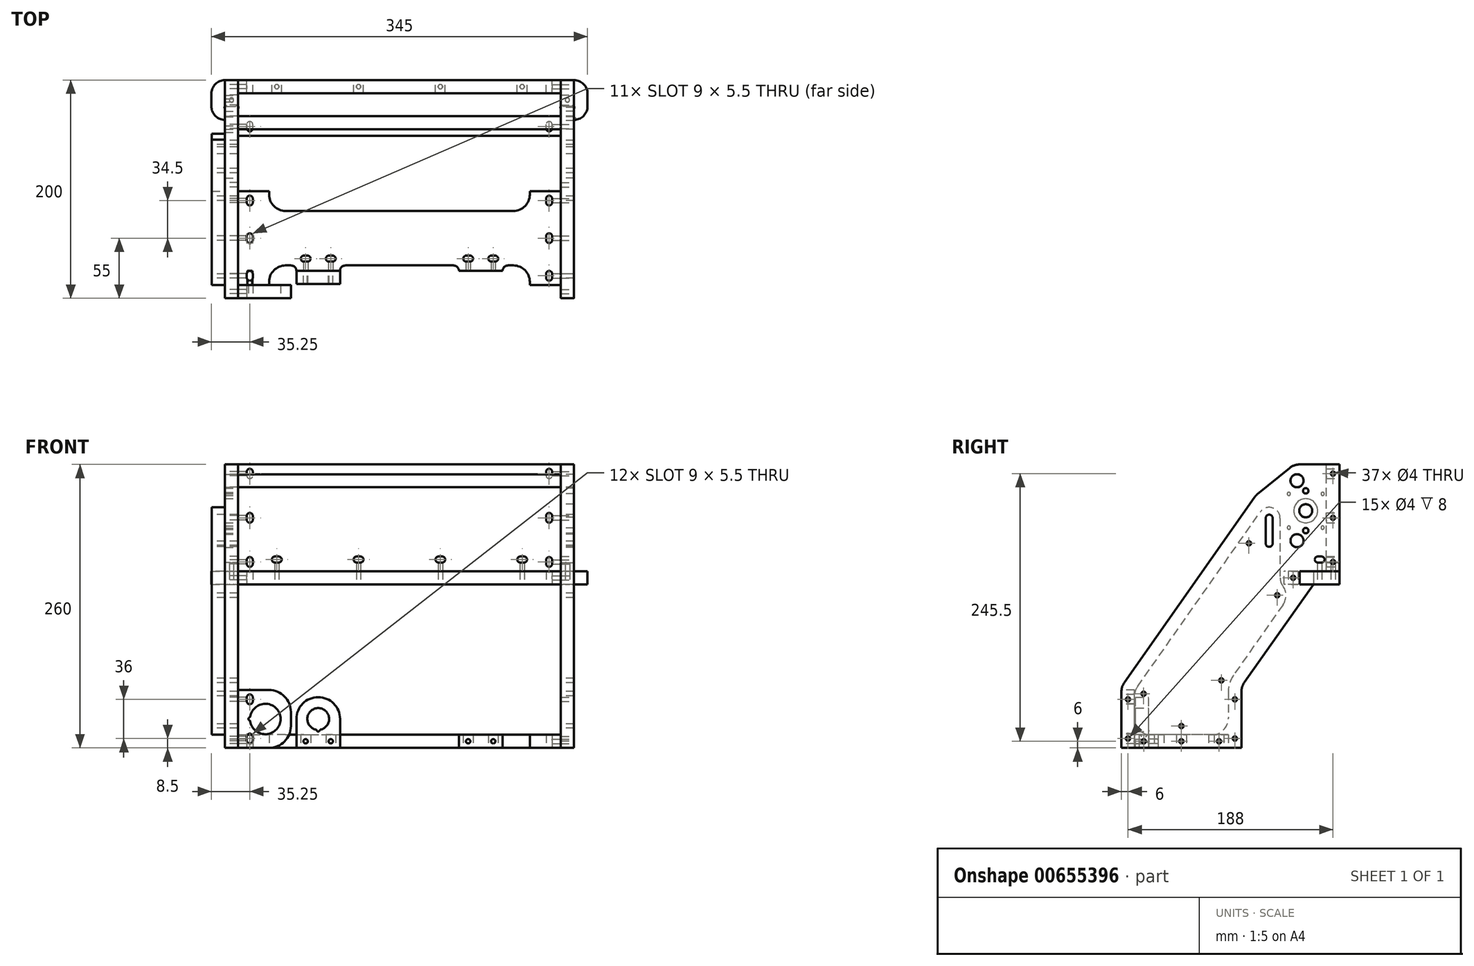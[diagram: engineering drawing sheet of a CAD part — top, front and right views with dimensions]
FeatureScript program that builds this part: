
annotation { "Feature Type Name" : "Feature", "Feature Type Description" : "" }
export const myFeature = defineFeature(function(context is Context, id is Id, definition is map)
    precondition{}
    {
        {
            var Q0;
            Q0=qCreatedBy(makeId("Front.planeOp"),FACE);
            var sketch = newSketch(context, id + "F0", { "sketchPlane" : qUnion([Q0])});
            skLineSegment(sketch, "E0.bottom", {"start": v(-148, 0) * mm, "end": v(148, 0) * mm});
            skLineSegment(sketch, "E0.top", {"start": v(-148, 98) * mm, "end": v(148, 98) * mm});
            skLineSegment(sketch, "E0.left", {"start": v(-148, 0) * mm, "end": v(-148, 98) * mm});
            skLineSegment(sketch, "E0.right", {"start": v(148, 0) * mm, "end": v(148, 98) * mm});
            skSolve(sketch);
        }
        {
            var Q0;
            Q0=qSketchRegion(id+"F0",true);
            extrude(context, id + "F1", {"entities" : qUnion([Q0]), "depth" : 12 * mm, "offsetDistance" : 25 * mm});
        }
        {
            var Q0;
            Q0=makeQuery(id+"F1.opExtrude","SWEPT_FACE",FACE,{"disambiguationData":[OSD([sQuery(id+"F0.wireOp",EDGE,"E0.left")])]});
            var sketch = newSketch(context, id + "F2", { "sketchPlane" : qUnion([Q0])});
            skLineSegment(sketch, "E1.bottom", {"start": v(0, 98) * mm, "end": v(56.7, 98) * mm});
            skLineSegment(sketch, "E1.top", {"start": v(90, -162) * mm, "end": v(200, -162) * mm});
            skLineSegment(sketch, "E1.right", {"start": v(56.7, 98) * mm, "end": v(200, -105.92) * mm});
            skLineSegment(sketch, "E2", {"start": v(200, -162) * mm, "end": v(200, -105.92) * mm});
            skLineSegment(sketch, "E3", {"start": v(24, -12) * mm, "end": v(90, -105.92) * mm});
            skLineSegment(sketch, "E4", {"start": v(0, 0) * mm, "end": v(0, 98) * mm});
            skLineSegment(sketch, "E5", {"start": v(90, -162) * mm, "end": v(90, -105.92) * mm});
            skLineSegment(sketch, "E6", {"start": v(0, 0) * mm, "end": v(24, 0) * mm});
            skLineSegment(sketch, "E7", {"start": v(24, 0) * mm, "end": v(24, -12) * mm});
            skSolve(sketch);
        }
        {
            var Q0;
            Q0=qSketchRegion(id+"F2",true);
            extrude(context, id + "F3", {"entities" : qUnion([Q0]), "depth" : 12 * mm, "offsetDistance" : 25 * mm});
        }
        {
            var Q0;
            Q0=makeQuery(id+"F3.opExtrude","CAP_FACE",FACE,{"disambiguationData":[OSD([sQuery(id+"F2.wireOp",EDGE,"E1.bottom"),sQuery(id+"F2.wireOp",EDGE,"E1.top"),sQuery(id+"F2.wireOp",EDGE,"E1.left"),sQuery(id+"F2.wireOp",EDGE,"E1.right"),sQuery(id+"F2.wireOp",EDGE,"E2"),sQuery(id+"F2.wireOp",EDGE,"2146645f-f5f1-4766-9391-dd441536dbd0.filletArc"),sQuery(id+"F2.wireOp",EDGE,"94e26631-0c9e-45e8-bca5-160914bd0a3d.filletArc")])],"isStart":true});
            var sketch = newSketch(context, id + "F4", { "sketchPlane" : qUnion([Q0])});
            skCircle(sketch, "E8", {"center": v(-39, 28) * mm, "radius": 5.97 * mm});
            skCircle(sketch, "E9", {"center": v(-39, 83) * mm, "radius": 5.97 * mm});
            skLineSegment(sketch, "E10", {"start": v(-39, 28) * mm, "end": v(-39, 83) * mm, "construction": true});
            skCircle(sketch, "E11", {"center": v(-31, 55.5) * mm, "radius": 11 * mm});
            skPoint(sketch, "E11.centerSnap0", {"position": v(-39, 55.5) * mm});
            skLineSegment(sketch, "E12.bottom", {"start": v(-15.5, 71) * mm, "end": v(-46.5, 71) * mm, "construction": true});
            skLineSegment(sketch, "E12.top", {"start": v(-15.5, 40) * mm, "end": v(-46.5, 40) * mm, "construction": true});
            skLineSegment(sketch, "E12.left", {"start": v(-15.5, 71) * mm, "end": v(-15.5, 40) * mm, "construction": true});
            skLineSegment(sketch, "E12.right", {"start": v(-46.5, 71) * mm, "end": v(-46.5, 40) * mm, "construction": true});
            skLineSegment(sketch, "E13", {"start": v(-31, 55.5) * mm, "end": v(-31, 71) * mm, "construction": true});
            skLineSegment(sketch, "E14", {"start": v(-15.5, 55.5) * mm, "end": v(-31, 55.5) * mm, "construction": true});
            skCircle(sketch, "E15", {"center": v(-46.5, 71) * mm, "radius": 1.5 * mm});
            skCircle(sketch, "E16.1.0", {"center": v(-46.5, 40) * mm, "radius": 1.5 * mm});
            skCircle(sketch, "E16.2.0", {"center": v(-15.5, 40) * mm, "radius": 1.5 * mm});
            skCircle(sketch, "E16.3.0", {"center": v(-15.5, 71) * mm, "radius": 1.5 * mm});
            skCircle(sketch, "E17", {"center": v(-31, 73.75) * mm, "radius": 2.5 * mm});
            skCircle(sketch, "E18.MirrorC", {"center": v(-31, 37.25) * mm, "radius": 2.5 * mm});
            skSolve(sketch);
        }
        {
            var Q0;
            Q0=qSketchRegion(id+"F4",true);
            extrude(context, id + "F5", {"entities" : qUnion([Q0]), "operationType" : NewBodyOperationType.REMOVE, "oppositeDirection" : true, "depth" : 25 * mm, "offsetDistance" : 25 * mm});
        }
        {
            var Q0;
            Q0=makeQuery(id+"F3.opExtrude","CAP_FACE",FACE,{"disambiguationData":[OSD([sQuery(id+"F2.wireOp",EDGE,"E1.bottom"),sQuery(id+"F2.wireOp",EDGE,"E1.top"),sQuery(id+"F2.wireOp",EDGE,"E1.left"),sQuery(id+"F2.wireOp",EDGE,"E1.right"),sQuery(id+"F2.wireOp",EDGE,"E2"),sQuery(id+"F2.wireOp",EDGE,"2146645f-f5f1-4766-9391-dd441536dbd0.filletArc"),sQuery(id+"F2.wireOp",EDGE,"94e26631-0c9e-45e8-bca5-160914bd0a3d.filletArc")])],"isStart":false});
            var sketch = newSketch(context, id + "F6", { "sketchPlane" : qUnion([Q0])});
            skCircle(sketch, "E19", {"center": v(39, 83) * mm, "radius": 6 * mm});
            skSolve(sketch);
        }
        {
            var Q0;
            Q0=qSketchRegion(id+"F6",true);
            extrude(context, id + "F7", {"entities" : qUnion([Q0]), "oppositeDirection" : true, "depth" : 320 * mm, "offsetDistance" : 25 * mm});
        }
        {
            var Q0;
            Q0=makeQuery(id+"F1.opExtrude","SWEPT_FACE",FACE,{"disambiguationData":[OSD([sQuery(id+"F0.wireOp",EDGE,"E0.right")])]});
            var sketch = newSketch(context, id + "F8", { "sketchPlane" : qUnion([Q0])});
            skCircle(sketch, "E20.0", {"center": v(-39, 83) * mm, "radius": 5.97 * mm});
            skCircle(sketch, "E21.0", {"center": v(-39, 28) * mm, "radius": 5.97 * mm});
            skLineSegment(sketch, "E22.1", {"start": v(-90, -105.92) * mm, "end": v(-24, -12) * mm});
            skLineSegment(sketch, "E22.5", {"start": v(0, 98) * mm, "end": v(-56.7, 98) * mm});
            skLineSegment(sketch, "E22.6", {"start": v(-56.7, 98) * mm, "end": v(-200, -105.92) * mm});
            skLineSegment(sketch, "E22.8", {"start": v(0, 0) * mm, "end": v(0, 98) * mm});
            skLineSegment(sketch, "E22.9", {"start": v(-200, -105.92) * mm, "end": v(-200, -162) * mm});
            skLineSegment(sketch, "E22.10", {"start": v(-200, -162) * mm, "end": v(-90, -162) * mm});
            skLineSegment(sketch, "E22.11", {"start": v(-90, -162) * mm, "end": v(-90, -105.92) * mm});
            skCircle(sketch, "E23.0", {"center": v(-31, 73.75) * mm, "radius": 2.5 * mm});
            skCircle(sketch, "E24.0", {"center": v(-31, 37.25) * mm, "radius": 2.5 * mm});
            skCircle(sketch, "E25.0", {"center": v(-31, 55.5) * mm, "radius": 6 * mm});
            skLineSegment(sketch, "E26", {"start": v(-24, -12) * mm, "end": v(-24, 0) * mm});
            skLineSegment(sketch, "E27", {"start": v(-24, 0) * mm, "end": v(0, 0) * mm});
            skSolve(sketch);
        }
        {
            var Q0;
            Q0=qSketchRegion(id+"F8",true);
            extrude(context, id + "F9", {"entities" : qUnion([Q0]), "depth" : 12 * mm, "offsetDistance" : 25 * mm});
        }
        {
            var Q0;
            Q0=makeQuery(id+"F3.opExtrude","SWEPT_FACE",FACE,{"disambiguationData":[OSD([sQuery(id+"F2.wireOp",EDGE,"E2")])]});
            var sketch = newSketch(context, id + "F10", { "sketchPlane" : qUnion([Q0])});
            skLineSegment(sketch, "E28.bottom", {"start": v(-148, -162) * mm, "end": v(-119.5, -162) * mm});
            skLineSegment(sketch, "E28.top", {"start": v(-148, -109) * mm, "end": v(-119.5, -109) * mm});
            skLineSegment(sketch, "E28.left", {"start": v(-148, -162) * mm, "end": v(-148, -109) * mm});
            skLineSegment(sketch, "E28.right", {"start": v(-99.5, -142) * mm, "end": v(-99.5, -129) * mm});
            skArc(sketch, "E29", {"start": v(-136.8, -137.7) * mm, "mid": v(-109.02, -135.5) * mm, "end": v(-136.8, -133.3) * mm});
            skPoint(sketch, "E29.centerSnap0", {"position": v(-148, -135.5) * mm});
            skPoint(sketch, "E29.centerSnap1", {"position": v(-123, -160.5) * mm});
            skArc(sketch, "E30.filletArc", {"start": v(-99.5, -129) * mm, "mid": v(-105.36, -114.86) * mm, "end": v(-119.5, -109) * mm});
            skArc(sketch, "E31.filletArc", {"start": v(-119.5, -162) * mm, "mid": v(-105.36, -156.14) * mm, "end": v(-99.5, -142) * mm});
            skArc(sketch, "E32", {"start": v(-137.46, -134.08) * mm, "mid": v(-138.47, -135.5) * mm, "end": v(-137.46, -136.92) * mm});
            skPoint(sketch, "E33.visualSharp", {"position": v(-136.9, -134) * mm});
            skArc(sketch, "E33.filletArc", {"start": v(-137.46, -134.08) * mm, "mid": v(-137.02, -133.78) * mm, "end": v(-136.8, -133.3) * mm});
            skPoint(sketch, "E34.visualSharp", {"position": v(-136.9, -137) * mm});
            skArc(sketch, "E34.filletArc", {"start": v(-136.8, -137.7) * mm, "mid": v(-137.02, -137.22) * mm, "end": v(-137.46, -136.92) * mm});
            skSolve(sketch);
        }
        {
            var Q0;
            Q0=qSketchRegion(id+"F10",true);
            extrude(context, id + "F11", {"entities" : qUnion([Q0]), "oppositeDirection" : true, "depth" : 12 * mm, "offsetDistance" : 25 * mm});
        }
        {
            var Q0;
            Q0=makeQuery(id+"F3.opExtrude","SWEPT_FACE",FACE,{"disambiguationData":[OSD([sQuery(id+"F2.wireOp",EDGE,"E1.top")])]});
            var sketch = newSketch(context, id + "F12", { "sketchPlane" : qUnion([Q0])});
            skLineSegment(sketch, "E35.bottom", {"start": v(-104.5, 170) * mm, "end": v(-99.5, 170) * mm});
            skLineSegment(sketch, "E35.top", {"start": v(-148, 145) * mm, "end": v(148, 145) * mm, "construction": true});
            skLineSegment(sketch, "E36.top", {"start": v(-148, 188) * mm, "end": v(-119.5, 188) * mm});
            skPoint(sketch, "E37", {"position": v(-148, 145) * mm});
            skLineSegment(sketch, "E38.trimOffspring", {"start": v(-119.5, 185) * mm, "end": v(-119.5, 188) * mm});
            skPoint(sketch, "E39.visualSharp", {"position": v(-119.5, 170) * mm});
            skArc(sketch, "E39.filletArc", {"start": v(-119.5, 185) * mm, "mid": v(-115.1, 174.4) * mm, "end": v(-104.5, 170) * mm});
            skLineSegment(sketch, "E40", {"start": v(-148, 188) * mm, "end": v(-148, 145) * mm});
            skLineSegment(sketch, "E41", {"start": v(0, 145) * mm, "end": v(0, 170) * mm, "construction": true});
            skLineSegment(sketch, "E42.MirrorCS", {"start": v(104.5, 170) * mm, "end": v(99.5, 170) * mm});
            skArc(sketch, "E43.MirrorCS", {"start": v(119.5, 185) * mm, "mid": v(115.1, 174.4) * mm, "end": v(104.5, 170) * mm});
            skLineSegment(sketch, "E44.MirrorCS", {"start": v(119.5, 185) * mm, "end": v(119.5, 188) * mm});
            skLineSegment(sketch, "E45.MirrorCS", {"start": v(148, 188) * mm, "end": v(119.5, 188) * mm});
            skLineSegment(sketch, "E46.MirrorCS", {"start": v(148, 188) * mm, "end": v(148, 145) * mm});
            skLineSegment(sketch, "E47.MirrorCS", {"start": v(-119.5, 105) * mm, "end": v(-119.5, 102) * mm});
            skLineSegment(sketch, "E48.MirrorCS", {"start": v(119.5, 105) * mm, "end": v(119.5, 102) * mm});
            skLineSegment(sketch, "E49.MirrorCS", {"start": v(-148, 102) * mm, "end": v(-119.5, 102) * mm});
            skLineSegment(sketch, "E50.MirrorCS", {"start": v(148, 102) * mm, "end": v(119.5, 102) * mm});
            skLineSegment(sketch, "E51.MirrorCS", {"start": v(148, 102) * mm, "end": v(148, 145) * mm});
            skLineSegment(sketch, "E52.MirrorCS", {"start": v(-104.5, 120) * mm, "end": v(0, 120) * mm});
            skArc(sketch, "E53.MirrorCS", {"start": v(119.5, 105) * mm, "mid": v(115.1, 115.6) * mm, "end": v(104.5, 120) * mm});
            skLineSegment(sketch, "E54.MirrorCS", {"start": v(104.5, 120) * mm, "end": v(0, 120) * mm});
            skPoint(sketch, "E55.MirrorP", {"position": v(-119.5, 120) * mm});
            skArc(sketch, "E56.MirrorCS", {"start": v(-119.5, 105) * mm, "mid": v(-115.1, 115.6) * mm, "end": v(-104.5, 120) * mm});
            skLineSegment(sketch, "E57.MirrorCS", {"start": v(-148, 102) * mm, "end": v(-148, 145) * mm});
            skLineSegment(sketch, "E58", {"start": v(-137.25, 108.75) * mm, "end": v(-137.25, 112.25) * mm, "construction": true});
            skArc(sketch, "E59.0.startCap", {"start": v(-134.5, 108.75) * mm, "mid": v(-137.25, 106) * mm, "end": v(-140, 108.75) * mm});
            skArc(sketch, "E59.0.endCap", {"start": v(-140, 112.25) * mm, "mid": v(-137.25, 115) * mm, "end": v(-134.5, 112.25) * mm});
            skLineSegment(sketch, "E59.0.left", {"start": v(-140, 108.75) * mm, "end": v(-140, 112.25) * mm});
            skLineSegment(sketch, "E59.0.right", {"start": v(-134.5, 108.75) * mm, "end": v(-134.5, 112.25) * mm});
            skArc(sketch, "E60.MirrorCS", {"start": v(-140, 177.75) * mm, "mid": v(-137.25, 175) * mm, "end": v(-134.5, 177.75) * mm});
            skLineSegment(sketch, "E61.MirrorCS", {"start": v(-134.5, 181.25) * mm, "end": v(-134.5, 177.75) * mm});
            skArc(sketch, "E62.MirrorCS", {"start": v(-140, 181.25) * mm, "mid": v(-137.25, 184) * mm, "end": v(-134.5, 181.25) * mm});
            skLineSegment(sketch, "E63.MirrorCS", {"start": v(-140, 181.25) * mm, "end": v(-140, 177.75) * mm});
            skLineSegment(sketch, "E64", {"start": v(-137.25, 143.25) * mm, "end": v(-137.25, 146.75) * mm, "construction": true});
            skArc(sketch, "E65.0.startCap", {"start": v(-134.5, 143.25) * mm, "mid": v(-137.25, 140.5) * mm, "end": v(-140, 143.25) * mm});
            skArc(sketch, "E65.0.endCap", {"start": v(-140, 146.75) * mm, "mid": v(-137.25, 149.5) * mm, "end": v(-134.5, 146.75) * mm});
            skLineSegment(sketch, "E65.0.left", {"start": v(-140, 143.25) * mm, "end": v(-140, 146.75) * mm});
            skLineSegment(sketch, "E65.0.right", {"start": v(-134.5, 143.25) * mm, "end": v(-134.5, 146.75) * mm});
            skPoint(sketch, "E66", {"position": v(-137.25, 145) * mm});
            skLineSegment(sketch, "E67.MirrorCS", {"start": v(137.25, 108.75) * mm, "end": v(137.25, 112.25) * mm, "construction": true});
            skLineSegment(sketch, "E68.MirrorCS", {"start": v(137.25, 143.25) * mm, "end": v(137.25, 146.75) * mm, "construction": true});
            skLineSegment(sketch, "E69.MirrorCS", {"start": v(134.5, 108.75) * mm, "end": v(134.5, 112.25) * mm});
            skPoint(sketch, "E70.MirrorP", {"position": v(137.25, 145) * mm});
            skLineSegment(sketch, "E71.MirrorCS", {"start": v(140, 181.25) * mm, "end": v(140, 177.75) * mm});
            skLineSegment(sketch, "E72.MirrorCS", {"start": v(140, 143.25) * mm, "end": v(140, 146.75) * mm});
            skLineSegment(sketch, "E73.MirrorCS", {"start": v(134.5, 181.25) * mm, "end": v(134.5, 177.75) * mm});
            skLineSegment(sketch, "E74.MirrorCS", {"start": v(140, 108.75) * mm, "end": v(140, 112.25) * mm});
            skLineSegment(sketch, "E75.MirrorCS", {"start": v(134.5, 143.25) * mm, "end": v(134.5, 146.75) * mm});
            skArc(sketch, "E76.MirrorCS", {"start": v(140, 112.25) * mm, "mid": v(137.25, 115) * mm, "end": v(134.5, 112.25) * mm});
            skArc(sketch, "E77.MirrorCS", {"start": v(140, 181.25) * mm, "mid": v(137.25, 184) * mm, "end": v(134.5, 181.25) * mm});
            skArc(sketch, "E78.MirrorCS", {"start": v(134.5, 108.75) * mm, "mid": v(137.25, 106) * mm, "end": v(140, 108.75) * mm});
            skArc(sketch, "E79.MirrorCS", {"start": v(140, 146.75) * mm, "mid": v(137.25, 149.5) * mm, "end": v(134.5, 146.75) * mm});
            skPoint(sketch, "E80.MirrorP", {"position": v(119.5, 120) * mm});
            skArc(sketch, "E81.MirrorCS", {"start": v(140, 177.75) * mm, "mid": v(137.25, 175) * mm, "end": v(134.5, 177.75) * mm});
            skPoint(sketch, "E82.MirrorP", {"position": v(119.5, 170) * mm});
            skArc(sketch, "E83.MirrorCS", {"start": v(134.5, 143.25) * mm, "mid": v(137.25, 140.5) * mm, "end": v(140, 143.25) * mm});
            skLineSegment(sketch, "E84", {"start": v(-94.5, 175) * mm, "end": v(-54.5, 175) * mm});
            skArc(sketch, "E85", {"start": v(-99.5, 170) * mm, "mid": v(-95.96, 171.46) * mm, "end": v(-94.5, 175) * mm});
            skPoint(sketch, "E86.orphan", {"position": v(0, 170) * mm});
            skArc(sketch, "E87.MirrorCS", {"start": v(-49.5, 170) * mm, "mid": v(-53.04, 171.46) * mm, "end": v(-54.5, 175) * mm});
            skLineSegment(sketch, "E88", {"start": v(-49.5, 170) * mm, "end": v(0, 170) * mm});
            skLineSegment(sketch, "E89.MirrorCS", {"start": v(49.5, 170) * mm, "end": v(0, 170) * mm});
            skArc(sketch, "E90.MirrorCS", {"start": v(49.5, 170) * mm, "mid": v(53.04, 171.46) * mm, "end": v(54.5, 175) * mm});
            skLineSegment(sketch, "E91.MirrorCS", {"start": v(94.5, 175) * mm, "end": v(54.5, 175) * mm});
            skArc(sketch, "E92.MirrorCS", {"start": v(99.5, 170) * mm, "mid": v(95.96, 171.46) * mm, "end": v(94.5, 175) * mm});
            skLineSegment(sketch, "E93", {"start": v(-87.75, 163.75) * mm, "end": v(-84.25, 163.75) * mm, "construction": true});
            skArc(sketch, "E94.0.startCap", {"start": v(-87.75, 161) * mm, "mid": v(-90.5, 163.75) * mm, "end": v(-87.75, 166.5) * mm});
            skArc(sketch, "E94.0.endCap", {"start": v(-84.25, 166.5) * mm, "mid": v(-81.5, 163.75) * mm, "end": v(-84.25, 161) * mm});
            skLineSegment(sketch, "E94.0.left", {"start": v(-87.75, 166.5) * mm, "end": v(-84.25, 166.5) * mm});
            skLineSegment(sketch, "E94.0.right", {"start": v(-87.75, 161) * mm, "end": v(-84.25, 161) * mm});
            skLineSegment(sketch, "E95", {"start": v(-94.5, 175) * mm, "end": v(-94.5, 170) * mm, "construction": true});
            skLineSegment(sketch, "E96", {"start": v(-74.5, 175) * mm, "end": v(-74.5, 172.2) * mm, "construction": true});
            skArc(sketch, "E97.MirrorCS", {"start": v(-64.75, 166.5) * mm, "mid": v(-67.5, 163.75) * mm, "end": v(-64.75, 161) * mm});
            skLineSegment(sketch, "E98.MirrorCS", {"start": v(-61.25, 161) * mm, "end": v(-64.75, 161) * mm});
            skLineSegment(sketch, "E99.MirrorCS", {"start": v(-61.25, 166.5) * mm, "end": v(-64.75, 166.5) * mm});
            skArc(sketch, "E100.MirrorCS", {"start": v(-61.25, 161) * mm, "mid": v(-58.5, 163.75) * mm, "end": v(-61.25, 166.5) * mm});
            skLineSegment(sketch, "E101.MirrorCS", {"start": v(61.25, 166.5) * mm, "end": v(64.75, 166.5) * mm});
            skLineSegment(sketch, "E102.MirrorCS", {"start": v(87.75, 166.5) * mm, "end": v(84.25, 166.5) * mm});
            skArc(sketch, "E103.MirrorCS", {"start": v(61.25, 161) * mm, "mid": v(58.5, 163.75) * mm, "end": v(61.25, 166.5) * mm});
            skLineSegment(sketch, "E104.MirrorCS", {"start": v(61.25, 161) * mm, "end": v(64.75, 161) * mm});
            skArc(sketch, "E105.MirrorCS", {"start": v(64.75, 166.5) * mm, "mid": v(67.5, 163.75) * mm, "end": v(64.75, 161) * mm});
            skArc(sketch, "E106.MirrorCS", {"start": v(84.25, 166.5) * mm, "mid": v(81.5, 163.75) * mm, "end": v(84.25, 161) * mm});
            skLineSegment(sketch, "E107.MirrorCS", {"start": v(87.75, 161) * mm, "end": v(84.25, 161) * mm});
            skArc(sketch, "E108.MirrorCS", {"start": v(87.75, 161) * mm, "mid": v(90.5, 163.75) * mm, "end": v(87.75, 166.5) * mm});
            skSolve(sketch);
        }
        {
            var Q0;
            Q0=qSketchRegion(id+"F12",true);
            extrude(context, id + "F13", {"entities" : qUnion([Q0]), "oppositeDirection" : true, "depth" : 12 * mm, "offsetDistance" : 25 * mm});
        }
        {
            var Q0;
            Q0=makeQuery(id+"F11.opExtrude","CAP_FACE",FACE,{"disambiguationData":[OSD([sQuery(id+"F10.wireOp",EDGE,"E28.bottom"),sQuery(id+"F10.wireOp",EDGE,"E28.top"),sQuery(id+"F10.wireOp",EDGE,"E28.left"),sQuery(id+"F10.wireOp",EDGE,"E28.right"),sQuery(id+"F10.wireOp",EDGE,"E29"),sQuery(id+"F10.wireOp",EDGE,"E30.filletArc"),sQuery(id+"F10.wireOp",EDGE,"E31.filletArc")])],"isStart":true});
            var sketch = newSketch(context, id + "F14", { "sketchPlane" : qUnion([Q0])});
            skLineSegment(sketch, "E109", {"start": v(-137.25, -115.75) * mm, "end": v(-137.25, -119.25) * mm, "construction": true});
            skArc(sketch, "E110.0.startCap", {"start": v(-140, -115.75) * mm, "mid": v(-137.25, -113) * mm, "end": v(-134.5, -115.75) * mm});
            skArc(sketch, "E110.0.endCap", {"start": v(-134.5, -119.25) * mm, "mid": v(-137.25, -122) * mm, "end": v(-140, -119.25) * mm});
            skLineSegment(sketch, "E110.0.left", {"start": v(-134.5, -115.75) * mm, "end": v(-134.5, -119.25) * mm});
            skLineSegment(sketch, "E110.0.right", {"start": v(-140, -115.75) * mm, "end": v(-140, -119.25) * mm});
            skLineSegment(sketch, "E111", {"start": v(-148, -135.5) * mm, "end": v(-136.97, -135.5) * mm, "construction": true});
            skLineSegment(sketch, "E112.MirrorCS", {"start": v(-134.5, -155.25) * mm, "end": v(-134.5, -151.75) * mm});
            skLineSegment(sketch, "E113.MirrorCS", {"start": v(-140, -155.25) * mm, "end": v(-140, -151.75) * mm});
            skArc(sketch, "E114.MirrorCS", {"start": v(-140, -155.25) * mm, "mid": v(-137.25, -158) * mm, "end": v(-134.5, -155.25) * mm});
            skArc(sketch, "E115.MirrorCS", {"start": v(-134.5, -151.75) * mm, "mid": v(-137.25, -149) * mm, "end": v(-140, -151.75) * mm});
            skSolve(sketch);
        }
        {
            var Q0;
            Q0=qSketchRegion(id+"F14",true);
            extrude(context, id + "F15", {"entities" : qUnion([Q0]), "operationType" : NewBodyOperationType.REMOVE, "oppositeDirection" : true, "depth" : 25 * mm, "offsetDistance" : 25 * mm});
        }
        {
            var Q0;
            Q0=makeQuery(id+"F1.opExtrude","SWEPT_FACE",FACE,{"disambiguationData":[OSD([sQuery(id+"F0.wireOp",EDGE,"E0.bottom")])]});
            var sketch = newSketch(context, id + "F16", { "sketchPlane" : qUnion([Q0])});
            skLineSegment(sketch, "E116", {"start": v(-160, 0) * mm, "end": v(160, 0) * mm});
            skLineSegment(sketch, "E117", {"start": v(-157.88, 24) * mm, "end": v(-150.12, 24) * mm});
            skLineSegment(sketch, "E118", {"start": v(-148, 26.12) * mm, "end": v(-148, 51) * mm});
            skLineSegment(sketch, "E119", {"start": v(-148, 51) * mm, "end": v(0, 51) * mm});
            skLineSegment(sketch, "E120", {"start": v(0, 51) * mm, "end": v(0, 0) * mm, "construction": true});
            skLineSegment(sketch, "E121.MirrorCS", {"start": v(148, 51) * mm, "end": v(0, 51) * mm});
            skLineSegment(sketch, "E122.MirrorCS", {"start": v(148, 26.12) * mm, "end": v(148, 51) * mm});
            skLineSegment(sketch, "E123.MirrorCS", {"start": v(157.88, 24) * mm, "end": v(150.12, 24) * mm});
            skArc(sketch, "E124", {"start": v(-172.5, 12.5) * mm, "mid": v(-168.84, 3.66) * mm, "end": v(-160, 0) * mm});
            skArc(sketch, "E125", {"start": v(-161.09, 36.45) * mm, "mid": v(-169.22, 32.45) * mm, "end": v(-172.5, 24) * mm});
            skLineSegment(sketch, "E126", {"start": v(-160, 26.12) * mm, "end": v(-160, 35.46) * mm});
            skLineSegment(sketch, "E127", {"start": v(-172.5, 12.5) * mm, "end": v(-172.5, 24) * mm});
            skPoint(sketch, "E127.startSnap0", {"position": v(-172.5, 24) * mm});
            skPoint(sketch, "E128.visualSharp", {"position": v(-160, 36.5) * mm});
            skArc(sketch, "E128.filletArc", {"start": v(-160, 35.46) * mm, "mid": v(-160.32, 36.2) * mm, "end": v(-161.09, 36.45) * mm});
            skArc(sketch, "E129.MirrorCS", {"start": v(160, 35.46) * mm, "mid": v(160.32, 36.2) * mm, "end": v(161.09, 36.45) * mm});
            skPoint(sketch, "E130.MirrorP", {"position": v(160, 36.5) * mm});
            skLineSegment(sketch, "E131.MirrorCS", {"start": v(172.5, 12.5) * mm, "end": v(172.5, 24) * mm});
            skArc(sketch, "E132.MirrorCS", {"start": v(161.09, 36.45) * mm, "mid": v(169.22, 32.45) * mm, "end": v(172.5, 24) * mm});
            skLineSegment(sketch, "E133.MirrorCS", {"start": v(160, 26.12) * mm, "end": v(160, 35.46) * mm});
            skPoint(sketch, "E134.MirrorP", {"position": v(172.5, 24) * mm});
            skArc(sketch, "E135.trimOffspring", {"start": v(172.5, 12.5) * mm, "mid": v(168.84, 3.66) * mm, "end": v(160, 0) * mm});
            skArc(sketch, "E136", {"start": v(-160, 26.12) * mm, "mid": v(-160, 24) * mm, "end": v(-157.88, 24) * mm});
            skLineSegment(sketch, "E137", {"start": v(-160, 26.12) * mm, "end": v(-160, 24) * mm, "construction": true});
            skLineSegment(sketch, "E138", {"start": v(-157.88, 24) * mm, "end": v(-160, 24) * mm, "construction": true});
            skArc(sketch, "E139.MirrorCS", {"start": v(-148, 26.12) * mm, "mid": v(-148, 24) * mm, "end": v(-150.12, 24) * mm});
            skArc(sketch, "E140.MirrorCS", {"start": v(160, 26.12) * mm, "mid": v(160, 24) * mm, "end": v(157.88, 24) * mm});
            skArc(sketch, "E141.MirrorCS", {"start": v(148, 26.12) * mm, "mid": v(148, 24) * mm, "end": v(150.12, 24) * mm});
            skSolve(sketch);
        }
        {
            var Q0;
            Q0=qSketchRegion(id+"F16",true);
            extrude(context, id + "F17", {"entities" : qUnion([Q0]), "depth" : 12 * mm, "offsetDistance" : 25 * mm});
        }
        {
            var Q0;
            Q0=makeQuery(id+"F3.opExtrude","CAP_FACE",FACE,{"disambiguationData":[OSD([sQuery(id+"F2.wireOp",EDGE,"E1.bottom"),sQuery(id+"F2.wireOp",EDGE,"E1.top"),sQuery(id+"F2.wireOp",EDGE,"E1.right"),sQuery(id+"F2.wireOp",EDGE,"E2"),sQuery(id+"F2.wireOp",EDGE,"94e26631-0c9e-45e8-bca5-160914bd0a3d.filletArc"),sQuery(id+"F2.wireOp",EDGE,"E3"),sQuery(id+"F2.wireOp",EDGE,"E4"),sQuery(id+"F2.wireOp",EDGE,"3c304bfc-2885-443d-81d9-234e97ae9333.filletArc"),sQuery(id+"F2.wireOp",EDGE,"E5"),sQuery(id+"F2.wireOp",EDGE,"930fecb7-9af6-459d-8abb-d03ba6c7b7a5.filletArc"),sQuery(id+"F2.wireOp",EDGE,"yWCbbJBZ-1GEx-dhOH-k0kd-LSXJYkVx6NrP"),sQuery(id+"F2.wireOp",EDGE,"cebc93dc-49be-47df-9592-c98bafc6a396.filletArc"),sQuery(id+"F2.wireOp",EDGE,"0R2F742G-mTnw-hJEY-WdgB-tpz7tOERiha1"),sQuery(id+"F2.wireOp",EDGE,"3aeea579-ff88-4944-83f2-f3d4fbf2bd07.filletArc"),sQuery(id+"F2.wireOp",EDGE,"c7c51ab0-1a95-4586-bb57-7b3897809644.filletArc")])],"isStart":false});
            var sketch = newSketch(context, id + "F18", { "sketchPlane" : qUnion([Q0])});
            skCircle(sketch, "E142", {"center": v(194, -153.5) * mm, "radius": 2 * mm});
            skCircle(sketch, "E143", {"center": v(194, -117.5) * mm, "radius": 2 * mm});
            skLineSegment(sketch, "E144", {"start": v(145, -162) * mm, "end": v(145, -142.37) * mm, "construction": true});
            skCircle(sketch, "E145.MirrorC", {"center": v(96, -117.5) * mm, "radius": 2 * mm});
            skCircle(sketch, "E146.MirrorC", {"center": v(96, -153.5) * mm, "radius": 2 * mm});
            skCircle(sketch, "E147", {"center": v(179.5, -156) * mm, "radius": 2 * mm});
            skCircle(sketch, "E148", {"center": v(145, -156) * mm, "radius": 2 * mm});
            skCircle(sketch, "E149.MirrorC", {"center": v(110.5, -156) * mm, "radius": 2 * mm});
            skCircle(sketch, "E150", {"center": v(6, 89.5) * mm, "radius": 2 * mm});
            skCircle(sketch, "E151.0.1.0", {"center": v(6, 49) * mm, "radius": 2 * mm});
            skCircle(sketch, "E151.0.2.0", {"center": v(6, 8.5) * mm, "radius": 2 * mm});
            skLineSegment(sketch, "E151.direction1", {"start": v(6, 89.5) * mm, "end": v(31, 89.5) * mm, "construction": true});
            skLineSegment(sketch, "E151.direction2", {"start": v(6, 89.5) * mm, "end": v(6, 49) * mm, "construction": true});
            skLineSegment(sketch, "E152", {"start": v(16.5, 10.75) * mm, "end": v(20, 10.75) * mm, "construction": true});
            skArc(sketch, "E153.0.startCap", {"start": v(16.5, 8) * mm, "mid": v(13.75, 10.75) * mm, "end": v(16.5, 13.5) * mm});
            skArc(sketch, "E153.0.endCap", {"start": v(20, 13.5) * mm, "mid": v(22.75, 10.75) * mm, "end": v(20, 8) * mm});
            skLineSegment(sketch, "E153.0.left", {"start": v(16.5, 13.5) * mm, "end": v(20, 13.5) * mm});
            skLineSegment(sketch, "E153.0.right", {"start": v(16.5, 8) * mm, "end": v(20, 8) * mm});
            skPoint(sketch, "E154", {"position": v(18.25, 10.75) * mm});
            skCircle(sketch, "E155", {"center": v(42.5, -6) * mm, "radius": 2 * mm});
            skPoint(sketch, "E155.centerSnap0", {"position": v(24, -6) * mm});
            skLineSegment(sketch, "E156", {"start": v(24, -6) * mm, "end": v(51, -6) * mm, "construction": true});
            skSolve(sketch);
        }
        {
            var Q0;
            Q0=qSketchRegion(id+"F18",true);
            extrude(context, id + "F19", {"entities" : qUnion([Q0]), "operationType" : NewBodyOperationType.REMOVE, "oppositeDirection" : true, "depth" : 21 * mm, "offsetDistance" : 25 * mm});
        }
        {
            var Q0;
            Q0=makeQuery(id+"F1.opExtrude","CAP_FACE",FACE,{"disambiguationData":[OSD([sQuery(id+"F0.wireOp",EDGE,"E0.bottom"),sQuery(id+"F0.wireOp",EDGE,"E0.top"),sQuery(id+"F0.wireOp",EDGE,"E0.left"),sQuery(id+"F0.wireOp",EDGE,"E0.right")])],"isStart":true});
            var sketch = newSketch(context, id + "F20", { "sketchPlane" : qUnion([Q0])});
            skLineSegment(sketch, "E157", {"start": v(137.25, 91.25) * mm, "end": v(137.25, 87.75) * mm, "construction": true});
            skArc(sketch, "E158.0.startCap", {"start": v(134.5, 91.25) * mm, "mid": v(137.25, 94) * mm, "end": v(140, 91.25) * mm});
            skArc(sketch, "E158.0.endCap", {"start": v(140, 87.75) * mm, "mid": v(137.25, 85) * mm, "end": v(134.5, 87.75) * mm});
            skLineSegment(sketch, "E158.0.left", {"start": v(140, 91.25) * mm, "end": v(140, 87.75) * mm});
            skLineSegment(sketch, "E158.0.right", {"start": v(134.5, 91.25) * mm, "end": v(134.5, 87.75) * mm});
            skArc(sketch, "E159.0.1.0", {"start": v(134.5, 50.75) * mm, "mid": v(137.25, 53.5) * mm, "end": v(140, 50.75) * mm});
            skLineSegment(sketch, "E159.0.1.1", {"start": v(140, 50.75) * mm, "end": v(140, 47.25) * mm});
            skArc(sketch, "E159.0.1.2", {"start": v(140, 47.25) * mm, "mid": v(137.25, 44.5) * mm, "end": v(134.5, 47.25) * mm});
            skLineSegment(sketch, "E159.0.1.3", {"start": v(134.5, 50.75) * mm, "end": v(134.5, 47.25) * mm});
            skArc(sketch, "E159.0.2.0", {"start": v(134.5, 10.25) * mm, "mid": v(137.25, 13) * mm, "end": v(140, 10.25) * mm});
            skLineSegment(sketch, "E159.0.2.1", {"start": v(140, 10.25) * mm, "end": v(140, 6.75) * mm});
            skArc(sketch, "E159.0.2.2", {"start": v(140, 6.75) * mm, "mid": v(137.25, 4) * mm, "end": v(134.5, 6.75) * mm});
            skLineSegment(sketch, "E159.0.2.3", {"start": v(134.5, 10.25) * mm, "end": v(134.5, 6.75) * mm});
            skLineSegment(sketch, "E159.direction1", {"start": v(134.5, 87.75) * mm, "end": v(159, 87.75) * mm, "construction": true});
            skLineSegment(sketch, "E159.direction2", {"start": v(134.5, 87.75) * mm, "end": v(134.5, 47.25) * mm, "construction": true});
            skLineSegment(sketch, "E160", {"start": v(0, 0) * mm, "end": v(0, 98) * mm, "construction": true});
            skLineSegment(sketch, "E161.MirrorCS", {"start": v(-134.5, 91.25) * mm, "end": v(-134.5, 87.75) * mm});
            skLineSegment(sketch, "E162.MirrorCS", {"start": v(-140, 91.25) * mm, "end": v(-140, 87.75) * mm});
            skLineSegment(sketch, "E163.MirrorCS", {"start": v(-134.5, 50.75) * mm, "end": v(-134.5, 47.25) * mm});
            skLineSegment(sketch, "E164.MirrorCS", {"start": v(-140, 50.75) * mm, "end": v(-140, 47.25) * mm});
            skLineSegment(sketch, "E165.MirrorCS", {"start": v(-140, 10.25) * mm, "end": v(-140, 6.75) * mm});
            skLineSegment(sketch, "E166.MirrorCS", {"start": v(-134.5, 10.25) * mm, "end": v(-134.5, 6.75) * mm});
            skArc(sketch, "E167.MirrorCS", {"start": v(-134.5, 91.25) * mm, "mid": v(-137.25, 94) * mm, "end": v(-140, 91.25) * mm});
            skArc(sketch, "E168.MirrorCS", {"start": v(-140, 87.75) * mm, "mid": v(-137.25, 85) * mm, "end": v(-134.5, 87.75) * mm});
            skArc(sketch, "E169.MirrorCS", {"start": v(-134.5, 50.75) * mm, "mid": v(-137.25, 53.5) * mm, "end": v(-140, 50.75) * mm});
            skArc(sketch, "E170.MirrorCS", {"start": v(-140, 47.25) * mm, "mid": v(-137.25, 44.5) * mm, "end": v(-134.5, 47.25) * mm});
            skArc(sketch, "E171.MirrorCS", {"start": v(-134.5, 10.25) * mm, "mid": v(-137.25, 13) * mm, "end": v(-140, 10.25) * mm});
            skArc(sketch, "E172.MirrorCS", {"start": v(-140, 6.75) * mm, "mid": v(-137.25, 4) * mm, "end": v(-134.5, 6.75) * mm});
            skLineSegment(sketch, "E173", {"start": v(-110.75, 10.75) * mm, "end": v(-114.25, 10.75) * mm, "construction": true});
            skArc(sketch, "E174.0.startCap", {"start": v(-110.75, 13.5) * mm, "mid": v(-108, 10.75) * mm, "end": v(-110.75, 8) * mm});
            skArc(sketch, "E174.0.endCap", {"start": v(-114.25, 8) * mm, "mid": v(-117, 10.75) * mm, "end": v(-114.25, 13.5) * mm});
            skLineSegment(sketch, "E174.0.left", {"start": v(-110.75, 8) * mm, "end": v(-114.25, 8) * mm});
            skLineSegment(sketch, "E174.0.right", {"start": v(-110.75, 13.5) * mm, "end": v(-114.25, 13.5) * mm});
            skArc(sketch, "E175.1.0.0", {"start": v(-39.25, 8) * mm, "mid": v(-42, 10.75) * mm, "end": v(-39.25, 13.5) * mm});
            skLineSegment(sketch, "E175.1.0.1", {"start": v(-35.75, 13.5) * mm, "end": v(-39.25, 13.5) * mm});
            skLineSegment(sketch, "E175.1.0.2", {"start": v(-35.75, 8) * mm, "end": v(-39.25, 8) * mm});
            skArc(sketch, "E175.1.0.3", {"start": v(-35.75, 13.5) * mm, "mid": v(-33, 10.75) * mm, "end": v(-35.75, 8) * mm});
            skArc(sketch, "E175.2.0.0", {"start": v(35.75, 8) * mm, "mid": v(33, 10.75) * mm, "end": v(35.75, 13.5) * mm});
            skLineSegment(sketch, "E175.2.0.1", {"start": v(39.25, 13.5) * mm, "end": v(35.75, 13.5) * mm});
            skLineSegment(sketch, "E175.2.0.2", {"start": v(39.25, 8) * mm, "end": v(35.75, 8) * mm});
            skArc(sketch, "E175.2.0.3", {"start": v(39.25, 13.5) * mm, "mid": v(42, 10.75) * mm, "end": v(39.25, 8) * mm});
            skArc(sketch, "E175.3.0.0", {"start": v(110.75, 8) * mm, "mid": v(108, 10.75) * mm, "end": v(110.75, 13.5) * mm});
            skLineSegment(sketch, "E175.3.0.1", {"start": v(114.25, 13.5) * mm, "end": v(110.75, 13.5) * mm});
            skLineSegment(sketch, "E175.3.0.2", {"start": v(114.25, 8) * mm, "end": v(110.75, 8) * mm});
            skArc(sketch, "E175.3.0.3", {"start": v(114.25, 13.5) * mm, "mid": v(117, 10.75) * mm, "end": v(114.25, 8) * mm});
            skLineSegment(sketch, "E175.direction1", {"start": v(-114.25, 8) * mm, "end": v(-39.25, 8) * mm, "construction": true});
            skPoint(sketch, "E176", {"position": v(-37.5, 13.5) * mm});
            skSolve(sketch);
        }
        {
            var Q0;
            Q0=qSketchRegion(id+"F20",true);
            extrude(context, id + "F21", {"entities" : qUnion([Q0]), "operationType" : NewBodyOperationType.REMOVE, "oppositeDirection" : true, "depth" : 25 * mm, "offsetDistance" : 25 * mm});
        }
        {
            var Q0;
            Q0=makeQuery(id+"F9.opExtrude","CAP_FACE",FACE,{"disambiguationData":[OSD([sQuery(id+"F8.wireOp",EDGE,"E20.0"),sQuery(id+"F8.wireOp",EDGE,"E21.0"),sQuery(id+"F8.wireOp",EDGE,"E22.0"),sQuery(id+"F8.wireOp",EDGE,"E22.1"),sQuery(id+"F8.wireOp",EDGE,"E22.2"),sQuery(id+"F8.wireOp",EDGE,"E22.3"),sQuery(id+"F8.wireOp",EDGE,"E22.5"),sQuery(id+"F8.wireOp",EDGE,"E22.6"),sQuery(id+"F8.wireOp",EDGE,"E22.7"),sQuery(id+"F8.wireOp",EDGE,"E22.8"),sQuery(id+"F8.wireOp",EDGE,"E22.9"),sQuery(id+"F8.wireOp",EDGE,"E22.10"),sQuery(id+"F8.wireOp",EDGE,"E22.11"),sQuery(id+"F8.wireOp",EDGE,"E22.12"),sQuery(id+"F8.wireOp",EDGE,"0fa0f1f6-a39c-456d-a7d0-3881c9b7fbf4.0"),sQuery(id+"F8.wireOp",EDGE,"0fa0f1f6-a39c-456d-a7d0-3881c9b7fbf4.2"),sQuery(id+"F8.wireOp",EDGE,"E23.0"),sQuery(id+"F8.wireOp",EDGE,"E24.0"),sQuery(id+"F8.wireOp",EDGE,"E25.0")])],"isStart":false});
            var sketch = newSketch(context, id + "F22", { "sketchPlane" : qUnion([Q0])});
            skCircle(sketch, "E177.0", {"center": v(-96, -117.5) * mm, "radius": 2 * mm});
            skCircle(sketch, "E178.0", {"center": v(-96, -153.5) * mm, "radius": 2 * mm});
            skCircle(sketch, "E179.0", {"center": v(-110.5, -156) * mm, "radius": 2 * mm});
            skCircle(sketch, "E180.0", {"center": v(-145, -156) * mm, "radius": 2 * mm});
            skCircle(sketch, "E181.0", {"center": v(-179.5, -156) * mm, "radius": 2 * mm});
            skCircle(sketch, "E182.0", {"center": v(-194, -153.5) * mm, "radius": 2 * mm});
            skCircle(sketch, "E183.0", {"center": v(-194, -117.5) * mm, "radius": 2 * mm});
            skCircle(sketch, "E184.0", {"center": v(-6, 8.5) * mm, "radius": 2 * mm});
            skCircle(sketch, "E185.0", {"center": v(-6, 49) * mm, "radius": 2 * mm});
            skCircle(sketch, "E186.0", {"center": v(-6, 89.5) * mm, "radius": 2 * mm});
            skCircle(sketch, "E187.0", {"center": v(-42.5, -6) * mm, "radius": 2 * mm});
            skLineSegment(sketch, "E188.0", {"start": v(-16.5, 8) * mm, "end": v(-20, 8) * mm});
            skArc(sketch, "E188.1", {"start": v(-16.5, 8) * mm, "mid": v(-13.75, 10.75) * mm, "end": v(-16.5, 13.5) * mm});
            skLineSegment(sketch, "E188.2", {"start": v(-16.5, 13.5) * mm, "end": v(-20, 13.5) * mm});
            skArc(sketch, "E188.3", {"start": v(-20, 13.5) * mm, "mid": v(-22.75, 10.75) * mm, "end": v(-20, 8) * mm});
            skSolve(sketch);
        }
        {
            var Q0;
            Q0=qSketchRegion(id+"F22",true);
            extrude(context, id + "F23", {"entities" : qUnion([Q0]), "operationType" : NewBodyOperationType.REMOVE, "oppositeDirection" : true, "depth" : 21 * mm, "offsetDistance" : 25 * mm});
        }
        {
            var Q0;
            Q0=makeQuery(id+"F3.opExtrude","SWEPT_EDGE",EDGE,{"disambiguationData":[OSD([sQuery(id+"F2.wireOp",EDGE,"E1.bottom"),sQuery(id+"F2.wireOp",EDGE,"E1.right")])]});
            chamfer(context, id + "F24", {"entities" : qUnion([Q0]), "chamferType" : ChamferType.TWO_OFFSETS, "width1" : 15 * mm, "oppositeDirection" : false, "width2" : 35 * mm, "tangentPropagation" : true});
        }
        {
            var Q0;
            Q0=makeQuery(id+"F9.opExtrude","SWEPT_EDGE",EDGE,{"disambiguationData":[OSD([sQuery(id+"F8.wireOp",EDGE,"E22.5"),sQuery(id+"F8.wireOp",EDGE,"E22.6")])]});
            chamfer(context, id + "F25", {"entities" : qUnion([Q0]), "chamferType" : ChamferType.TWO_OFFSETS, "width1" : 35 * mm, "oppositeDirection" : false, "width2" : 15 * mm, "tangentPropagation" : true});
        }
        {
            var Q0;
            Q0=makeQuery(id+"F3.opExtrude","SWEPT_EDGE",EDGE,{"disambiguationData":[OSD([sQuery(id+"F2.wireOp",EDGE,"E1.right"),sQuery(id+"F2.wireOp",EDGE,"E2")])]});
            var Q1;
            Q1=makeQuery(id+"F9.opExtrude","SWEPT_EDGE",EDGE,{"disambiguationData":[OSD([sQuery(id+"F8.wireOp",EDGE,"E22.6"),sQuery(id+"F8.wireOp",EDGE,"E22.9")])]});
            var Q2;
            Q2=makeQuery(id+"F3.opExtrude","SWEPT_EDGE",EDGE,{"disambiguationData":[OSD([sQuery(id+"F2.wireOp",EDGE,"E3"),sQuery(id+"F2.wireOp",EDGE,"E5")])]});
            var Q3;
            Q3=makeQuery(id+"F9.opExtrude","SWEPT_EDGE",EDGE,{"disambiguationData":[OSD([sQuery(id+"F8.wireOp",EDGE,"E22.1"),sQuery(id+"F8.wireOp",EDGE,"E22.11")])]});
            var Q4;
            {var subQ0=sQuery(id+"F2.wireOp",EDGE,"E1.bottom");Q4=makeQuery(id+"F24.opChamfer","BLEND_EDGE",EDGE,{"blendedFrom":[makeQuery(id+"F3.opExtrude","SWEPT_EDGE",EDGE,{"disambiguationData":[OSD([subQ0,sQuery(id+"F2.wireOp",EDGE,"E1.right")])]}),makeQuery(id+"F3.opExtrude","SWEPT_FACE",FACE,{"disambiguationData":[OSD([subQ0])]})],"blendedInto":[makeQuery(id+"F3.opExtrude","SWEPT_FACE",FACE,{"disambiguationData":[OSD([subQ0])]})]});}
            var Q5;
            {var subQ0=sQuery(id+"F2.wireOp",EDGE,"E1.right");Q5=makeQuery(id+"F24.opChamfer","BLEND_EDGE",EDGE,{"blendedFrom":[makeQuery(id+"F3.opExtrude","SWEPT_EDGE",EDGE,{"disambiguationData":[OSD([sQuery(id+"F2.wireOp",EDGE,"E1.bottom"),subQ0])]}),makeQuery(id+"F3.opExtrude","SWEPT_FACE",FACE,{"disambiguationData":[OSD([subQ0])]})],"blendedInto":[makeQuery(id+"F3.opExtrude","SWEPT_FACE",FACE,{"disambiguationData":[OSD([subQ0])]})]});}
            var Q6;
            {var subQ0=sQuery(id+"F8.wireOp",EDGE,"E22.5");Q6=makeQuery(id+"F25.opChamfer","BLEND_EDGE",EDGE,{"blendedFrom":[makeQuery(id+"F9.opExtrude","SWEPT_EDGE",EDGE,{"disambiguationData":[OSD([subQ0,sQuery(id+"F8.wireOp",EDGE,"E22.6")])]}),makeQuery(id+"F9.opExtrude","SWEPT_FACE",FACE,{"disambiguationData":[OSD([subQ0])]})],"blendedInto":[makeQuery(id+"F9.opExtrude","SWEPT_FACE",FACE,{"disambiguationData":[OSD([subQ0])]})]});}
            var Q7;
            {var subQ0=sQuery(id+"F8.wireOp",EDGE,"E22.6");Q7=makeQuery(id+"F25.opChamfer","BLEND_EDGE",EDGE,{"blendedFrom":[makeQuery(id+"F9.opExtrude","SWEPT_EDGE",EDGE,{"disambiguationData":[OSD([sQuery(id+"F8.wireOp",EDGE,"E22.5"),subQ0])]}),makeQuery(id+"F9.opExtrude","SWEPT_FACE",FACE,{"disambiguationData":[OSD([subQ0])]})],"blendedInto":[makeQuery(id+"F9.opExtrude","SWEPT_FACE",FACE,{"disambiguationData":[OSD([subQ0])]})]});}
            fillet(context, id + "F26", {"entities" : qUnion([Q0, Q1, Q2, Q3, Q4, Q5, Q6, Q7]), "radius" : 15 * mm, "tangentPropagation" : true, "allowEdgeOverflow" : false});
        }
        {
            var Q0;
            Q0=makeQuery(id+"F17.opExtrude","CAP_FACE",FACE,{"disambiguationData":[OSD([sQuery(id+"F16.wireOp",EDGE,"E116"),sQuery(id+"F16.wireOp",EDGE,"cxGHmkkV-L3Ph-Ebet-9txR-TFSqyXeuAXPF"),sQuery(id+"F16.wireOp",EDGE,"E117"),sQuery(id+"F16.wireOp",EDGE,"E118"),sQuery(id+"F16.wireOp",EDGE,"E119"),sQuery(id+"F16.wireOp",EDGE,"3yAaN058-1MfD-fWh8-1EEW-61dTXkiedIJ9"),sQuery(id+"F16.wireOp",EDGE,"fbd00211-0dd4-45b7-a840-197ed4c294e40.MirrorC"),sQuery(id+"F16.wireOp",EDGE,"E121.MirrorCS"),sQuery(id+"F16.wireOp",EDGE,"E122.MirrorCS"),sQuery(id+"F16.wireOp",EDGE,"E123.MirrorCS"),sQuery(id+"F16.wireOp",EDGE,"fbd00211-0dd4-45b7-a840-197ed4c294e44.MirrorCS")])],"isStart":false});
            var sketch = newSketch(context, id + "F27", { "sketchPlane" : qUnion([Q0])});
            skCircle(sketch, "E189", {"center": v(-154, 18.25) * mm, "radius": 2 * mm});
            skLineSegment(sketch, "E190", {"start": v(-137.25, 44.25) * mm, "end": v(-137.25, 40.75) * mm, "construction": true});
            skArc(sketch, "E191.0.startCap", {"start": v(-140, 44.25) * mm, "mid": v(-137.25, 47) * mm, "end": v(-134.5, 44.25) * mm});
            skArc(sketch, "E191.0.endCap", {"start": v(-134.5, 40.75) * mm, "mid": v(-137.25, 38) * mm, "end": v(-140, 40.75) * mm});
            skLineSegment(sketch, "E191.0.left", {"start": v(-134.5, 44.25) * mm, "end": v(-134.5, 40.75) * mm});
            skLineSegment(sketch, "E191.0.right", {"start": v(-140, 44.25) * mm, "end": v(-140, 40.75) * mm});
            skLineSegment(sketch, "E192", {"start": v(0, 0) * mm, "end": v(0, 51) * mm, "construction": true});
            skCircle(sketch, "E193.MirrorC", {"center": v(154, 18.25) * mm, "radius": 2 * mm});
            skLineSegment(sketch, "E194.MirrorCS", {"start": v(140, 44.25) * mm, "end": v(140, 40.75) * mm});
            skLineSegment(sketch, "E195.MirrorCS", {"start": v(134.5, 44.25) * mm, "end": v(134.5, 40.75) * mm});
            skArc(sketch, "E196.MirrorCS", {"start": v(134.5, 40.75) * mm, "mid": v(137.25, 38) * mm, "end": v(140, 40.75) * mm});
            skArc(sketch, "E197.MirrorCS", {"start": v(140, 44.25) * mm, "mid": v(137.25, 47) * mm, "end": v(134.5, 44.25) * mm});
            skCircle(sketch, "E198", {"center": v(-112.5, 6) * mm, "radius": 2 * mm});
            skCircle(sketch, "E199.1.0.0", {"center": v(-37.5, 6) * mm, "radius": 2 * mm});
            skCircle(sketch, "E199.2.0.0", {"center": v(37.5, 6) * mm, "radius": 2 * mm});
            skCircle(sketch, "E199.3.0.0", {"center": v(112.5, 6) * mm, "radius": 2 * mm});
            skLineSegment(sketch, "E199.direction1", {"start": v(-112.5, 6) * mm, "end": v(-37.5, 6) * mm, "construction": true});
            skSolve(sketch);
        }
        {
            var Q0;
            Q0=qSketchRegion(id+"F27",true);
            extrude(context, id + "F28", {"entities" : qUnion([Q0]), "operationType" : NewBodyOperationType.REMOVE, "oppositeDirection" : true, "depth" : 21 * mm, "offsetDistance" : 25 * mm});
        }
        {
            var Q0;
            Q0=makeQuery(id+"F3.opExtrude","CAP_FACE",FACE,{"disambiguationData":[OSD([sQuery(id+"F2.wireOp",EDGE,"E1.bottom"),sQuery(id+"F2.wireOp",EDGE,"E1.top"),sQuery(id+"F2.wireOp",EDGE,"E1.right"),sQuery(id+"F2.wireOp",EDGE,"E2"),sQuery(id+"F2.wireOp",EDGE,"E3"),sQuery(id+"F2.wireOp",EDGE,"E4"),sQuery(id+"F2.wireOp",EDGE,"E5"),sQuery(id+"F2.wireOp",EDGE,"E6"),sQuery(id+"F2.wireOp",EDGE,"E7")])],"isStart":false});
            var sketch = newSketch(context, id + "F29", { "sketchPlane" : qUnion([Q0])});
            skLineSegment(sketch, "E200.1", {"start": v(188, -150) * mm, "end": v(188, -114.46) * mm});
            skLineSegment(sketch, "E200.2", {"start": v(102, -150) * mm, "end": v(188, -150) * mm});
            skLineSegment(sketch, "E200.10", {"start": v(185.27, -105.83) * mm, "end": v(72.68, 54.39) * mm});
            skLineSegment(sketch, "E200.11", {"start": v(42.88, -18) * mm, "end": v(97.1, -95.14) * mm});
            skArc(sketch, "E200.12", {"start": v(97.1, -95.14) * mm, "mid": v(100.74, -102.52) * mm, "end": v(102, -110.66) * mm});
            skLineSegment(sketch, "E200.13", {"start": v(102, -110.66) * mm, "end": v(102, -150) * mm});
            skArc(sketch, "E201.0", {"start": v(42.88, -18) * mm, "mid": v(51.12, -14.35) * mm, "end": v(54.5, -6) * mm});
            skLineSegment(sketch, "E202", {"start": v(54.5, 48.64) * mm, "end": v(54.5, -6) * mm});
            skArc(sketch, "E203.filletArc", {"start": v(72.68, 54.39) * mm, "mid": v(61.48, 58.17) * mm, "end": v(54.5, 48.64) * mm});
            skArc(sketch, "E204.filletArc", {"start": v(188, -114.46) * mm, "mid": v(187.3, -109.94) * mm, "end": v(185.27, -105.83) * mm});
            skSolve(sketch);
        }
        {
            var Q0;
            Q0=qSketchRegion(id+"F29",true);
            extrude(context, id + "F30", {"entities" : qUnion([Q0]), "depth" : 12 * mm, "offsetDistance" : 25 * mm});
        }
        {
            var Q0;
            Q0=makeQuery(id+"F30.opExtrude","SWEPT_EDGE",EDGE,{"disambiguationData":[OSD([sQuery(id+"F29.wireOp",EDGE,"E200.11"),sQuery(id+"F29.wireOp",EDGE,"E201.0")])]});
            var Q1;
            Q1=makeQuery(id+"F30.opExtrude","SWEPT_EDGE",EDGE,{"disambiguationData":[OSD([sQuery(id+"F29.wireOp",EDGE,"E200.2"),sQuery(id+"F29.wireOp",EDGE,"E200.13")])]});
            var Q2;
            Q2=makeQuery(id+"F30.opExtrude","SWEPT_EDGE",EDGE,{"disambiguationData":[OSD([sQuery(id+"F29.wireOp",EDGE,"E200.1"),sQuery(id+"F29.wireOp",EDGE,"E200.2")])]});
            fillet(context, id + "F31", {"entities" : qUnion([Q0, Q1, Q2]), "radius" : 15 * mm, "tangentPropagation" : true, "allowEdgeOverflow" : false});
        }
        {
            var Q0;
            Q0=makeQuery(id+"F30.opExtrude","CAP_FACE",FACE,{"disambiguationData":[OSD([sQuery(id+"F29.wireOp",EDGE,"E200.1"),sQuery(id+"F29.wireOp",EDGE,"E200.2"),sQuery(id+"F29.wireOp",EDGE,"E200.10"),sQuery(id+"F29.wireOp",EDGE,"E200.11"),sQuery(id+"F29.wireOp",EDGE,"E200.12"),sQuery(id+"F29.wireOp",EDGE,"E200.13"),sQuery(id+"F29.wireOp",EDGE,"E201.0"),sQuery(id+"F29.wireOp",EDGE,"E202"),sQuery(id+"F29.wireOp",EDGE,"E203.filletArc"),sQuery(id+"F29.wireOp",EDGE,"E204.filletArc")])],"isStart":false});
            var sketch = newSketch(context, id + "F32", { "sketchPlane" : qUnion([Q0])});
            skLineSegment(sketch, "E205", {"start": v(64.5, 48.64) * mm, "end": v(64.5, 25.64) * mm, "construction": true});
            skArc(sketch, "E206.0.startCap", {"start": v(61.25, 48.64) * mm, "mid": v(64.5, 51.89) * mm, "end": v(67.75, 48.64) * mm});
            skArc(sketch, "E206.0.endCap", {"start": v(67.75, 25.64) * mm, "mid": v(64.5, 22.39) * mm, "end": v(61.25, 25.64) * mm});
            skLineSegment(sketch, "E206.0.left", {"start": v(67.75, 48.64) * mm, "end": v(67.75, 25.64) * mm});
            skLineSegment(sketch, "E206.0.right", {"start": v(61.25, 48.64) * mm, "end": v(61.25, 25.64) * mm});
            skCircle(sketch, "E207", {"center": v(57.14, -22.05) * mm, "radius": 2 * mm});
            skCircle(sketch, "E208", {"center": v(108.37, -100.11) * mm, "radius": 2 * mm});
            skCircle(sketch, "E209", {"center": v(145, -142) * mm, "radius": 2 * mm});
            skCircle(sketch, "E210", {"center": v(179.67, -112.35) * mm, "radius": 2 * mm});
            skCircle(sketch, "E211", {"center": v(83.1, 25.64) * mm, "radius": 2 * mm});
            skLineSegment(sketch, "E212.0", {"start": v(62.5, 48.64) * mm, "end": v(62.5, -6) * mm, "construction": true});
            skArc(sketch, "E212.1", {"start": v(66.14, 49.79) * mm, "mid": v(63.9, 50.54) * mm, "end": v(62.5, 48.64) * mm, "construction": true});
            skLineSegment(sketch, "E212.2", {"start": v(110, -110.66) * mm, "end": v(110, -135) * mm, "construction": true});
            skArc(sketch, "E212.3", {"start": v(103.64, -90.54) * mm, "mid": v(108.37, -100.11) * mm, "end": v(110, -110.66) * mm, "construction": true});
            skLineSegment(sketch, "E212.4", {"start": v(58.4, -26.18) * mm, "end": v(103.64, -90.54) * mm, "construction": true});
            skArc(sketch, "E212.5", {"start": v(58.53, -17.97) * mm, "mid": v(57.14, -22.05) * mm, "end": v(58.4, -26.18) * mm, "construction": true});
            skArc(sketch, "E212.6", {"start": v(110, -135) * mm, "mid": v(112.05, -139.95) * mm, "end": v(117, -142) * mm, "construction": true});
            skLineSegment(sketch, "E212.7", {"start": v(117, -142) * mm, "end": v(173, -142) * mm, "construction": true});
            skArc(sketch, "E212.8", {"start": v(62.5, -6) * mm, "mid": v(61.48, -12.3) * mm, "end": v(58.53, -17.97) * mm, "construction": true});
            skArc(sketch, "E212.9", {"start": v(173, -142) * mm, "mid": v(177.95, -139.95) * mm, "end": v(180, -135) * mm, "construction": true});
            skLineSegment(sketch, "E212.10", {"start": v(180, -135) * mm, "end": v(180, -114.46) * mm, "construction": true});
            skArc(sketch, "E212.11", {"start": v(180, -114.46) * mm, "mid": v(179.67, -112.35) * mm, "end": v(178.73, -110.43) * mm, "construction": true});
            skLineSegment(sketch, "E212.12", {"start": v(178.73, -110.43) * mm, "end": v(66.14, 49.79) * mm, "construction": true});
            skLineSegment(sketch, "E213", {"start": v(64.5, 25.64) * mm, "end": v(83.1, 25.64) * mm, "construction": true});
            skSolve(sketch);
        }
        {
            var Q0;
            Q0=qSketchRegion(id+"F32",true);
            extrude(context, id + "F33", {"entities" : qUnion([Q0]), "operationType" : NewBodyOperationType.REMOVE, "endBound" : BoundingType.THROUGH_ALL, "oppositeDirection" : true, "depth" : 25 * mm, "offsetDistance" : 25 * mm});
        }
        {
            var Q0;
            Q0=makeQuery(id+"F13.opExtrude","SWEPT_FACE",FACE,{"disambiguationData":[OSD([sQuery(id+"F12.wireOp",EDGE,"E84"),sQuery(id+"F12.wireOp",EDGE,"5ef5005f-9529-4792-9d74-6e6948cf13f80.MirrorCS")])]});
            var sketch = newSketch(context, id + "F34", { "sketchPlane" : qUnion([Q0])});
            skLineSegment(sketch, "E214.left", {"start": v(-94.5, -162) * mm, "end": v(-94.5, -135.5) * mm});
            skLineSegment(sketch, "E214.right", {"start": v(-54.5, -162) * mm, "end": v(-54.5, -135.5) * mm});
            skPoint(sketch, "E215.visualSharp", {"position": v(-94.5, -115.02) * mm});
            skCircle(sketch, "E216", {"center": v(-86, -156) * mm, "radius": 2 * mm});
            skCircle(sketch, "E217", {"center": v(-63, -156) * mm, "radius": 2 * mm});
            skArc(sketch, "E218", {"start": v(-54.5, -135.5) * mm, "mid": v(-74.5, -115.5) * mm, "end": v(-94.5, -135.5) * mm});
            skPoint(sketch, "E218.centerSnap0", {"position": v(-74.5, -150) * mm});
            skLineSegment(sketch, "E219", {"start": v(-94.5, -162) * mm, "end": v(-54.5, -162) * mm});
            skArc(sketch, "E220", {"start": v(-72.33, -145.24) * mm, "mid": v(-74.5, -125.53) * mm, "end": v(-76.67, -145.24) * mm});
            skArc(sketch, "E221", {"start": v(-75.93, -145.92) * mm, "mid": v(-74.5, -146.98) * mm, "end": v(-73.07, -145.92) * mm});
            skPoint(sketch, "E222.visualSharp", {"position": v(-76, -145.36) * mm});
            skArc(sketch, "E222.filletArc", {"start": v(-75.93, -145.92) * mm, "mid": v(-76.21, -145.48) * mm, "end": v(-76.67, -145.24) * mm});
            skPoint(sketch, "E223.visualSharp", {"position": v(-73, -145.36) * mm});
            skArc(sketch, "E223.filletArc", {"start": v(-72.33, -145.24) * mm, "mid": v(-72.79, -145.48) * mm, "end": v(-73.07, -145.92) * mm});
            skSolve(sketch);
        }
        {
            var Q0;
            Q0=qSketchRegion(id+"F34",true);
            extrude(context, id + "F35", {"entities" : qUnion([Q0]), "depth" : 12 * mm, "offsetDistance" : 25 * mm});
        }
        {
            var Q0;
            Q0=makeQuery(id+"F13.opExtrude","SWEPT_FACE",FACE,{"disambiguationData":[OSD([sQuery(id+"F12.wireOp",EDGE,"E91.MirrorCS")])]});
            var sketch = newSketch(context, id + "F36", { "sketchPlane" : qUnion([Q0])});
            skCircle(sketch, "E224.0", {"center": v(-86, -156) * mm, "radius": 2 * mm});
            skCircle(sketch, "E225.0", {"center": v(-63, -156) * mm, "radius": 2 * mm});
            skLineSegment(sketch, "E226", {"start": v(0, -165.2) * mm, "end": v(0, -150) * mm, "construction": true});
            skCircle(sketch, "E227.MirrorC", {"center": v(86, -156) * mm, "radius": 2 * mm});
            skCircle(sketch, "E228.MirrorC", {"center": v(63, -156) * mm, "radius": 2 * mm});
            skSolve(sketch);
        }
        {
            var Q0;
            Q0=qSketchRegion(id+"F36",true);
            extrude(context, id + "F37", {"entities" : qUnion([Q0]), "operationType" : NewBodyOperationType.REMOVE, "oppositeDirection" : true, "depth" : 10 * mm, "offsetDistance" : 25 * mm});
        }
        {
            var Q0;
            Q0=makeQuery(id+"F17.opExtrude","SWEPT_EDGE",EDGE,{"disambiguationData":[OSD([sQuery(id+"F16.wireOp",EDGE,"E133.MirrorCS"),sQuery(id+"F16.wireOp",EDGE,"E140.MirrorCS")])]});
            var Q1;
            Q1=makeQuery(id+"F17.opExtrude","SWEPT_EDGE",EDGE,{"disambiguationData":[OSD([sQuery(id+"F16.wireOp",EDGE,"E123.MirrorCS"),sQuery(id+"F16.wireOp",EDGE,"E140.MirrorCS")])]});
            var Q2;
            Q2=makeQuery(id+"F17.opExtrude","SWEPT_EDGE",EDGE,{"disambiguationData":[OSD([sQuery(id+"F16.wireOp",EDGE,"E123.MirrorCS"),sQuery(id+"F16.wireOp",EDGE,"E141.MirrorCS")])]});
            var Q3;
            Q3=makeQuery(id+"F17.opExtrude","SWEPT_EDGE",EDGE,{"disambiguationData":[OSD([sQuery(id+"F16.wireOp",EDGE,"E122.MirrorCS"),sQuery(id+"F16.wireOp",EDGE,"E141.MirrorCS")])]});
            var Q4;
            Q4=makeQuery(id+"F17.opExtrude","SWEPT_EDGE",EDGE,{"disambiguationData":[OSD([sQuery(id+"F16.wireOp",EDGE,"E126"),sQuery(id+"F16.wireOp",EDGE,"E136")])]});
            var Q5;
            Q5=makeQuery(id+"F17.opExtrude","SWEPT_EDGE",EDGE,{"disambiguationData":[OSD([sQuery(id+"F16.wireOp",EDGE,"E117"),sQuery(id+"F16.wireOp",EDGE,"E136")])]});
            var Q6;
            Q6=makeQuery(id+"F17.opExtrude","SWEPT_EDGE",EDGE,{"disambiguationData":[OSD([sQuery(id+"F16.wireOp",EDGE,"E117"),sQuery(id+"F16.wireOp",EDGE,"E139.MirrorCS")])]});
            var Q7;
            Q7=makeQuery(id+"F17.opExtrude","SWEPT_EDGE",EDGE,{"disambiguationData":[OSD([sQuery(id+"F16.wireOp",EDGE,"E118"),sQuery(id+"F16.wireOp",EDGE,"E139.MirrorCS")])]});
            fillet(context, id + "F38", {"entities" : qUnion([Q0, Q1, Q2, Q3, Q4, Q5, Q6, Q7]), "radius" : 1 * mm, "tangentPropagation" : true, "allowEdgeOverflow" : false});
        }
    });
